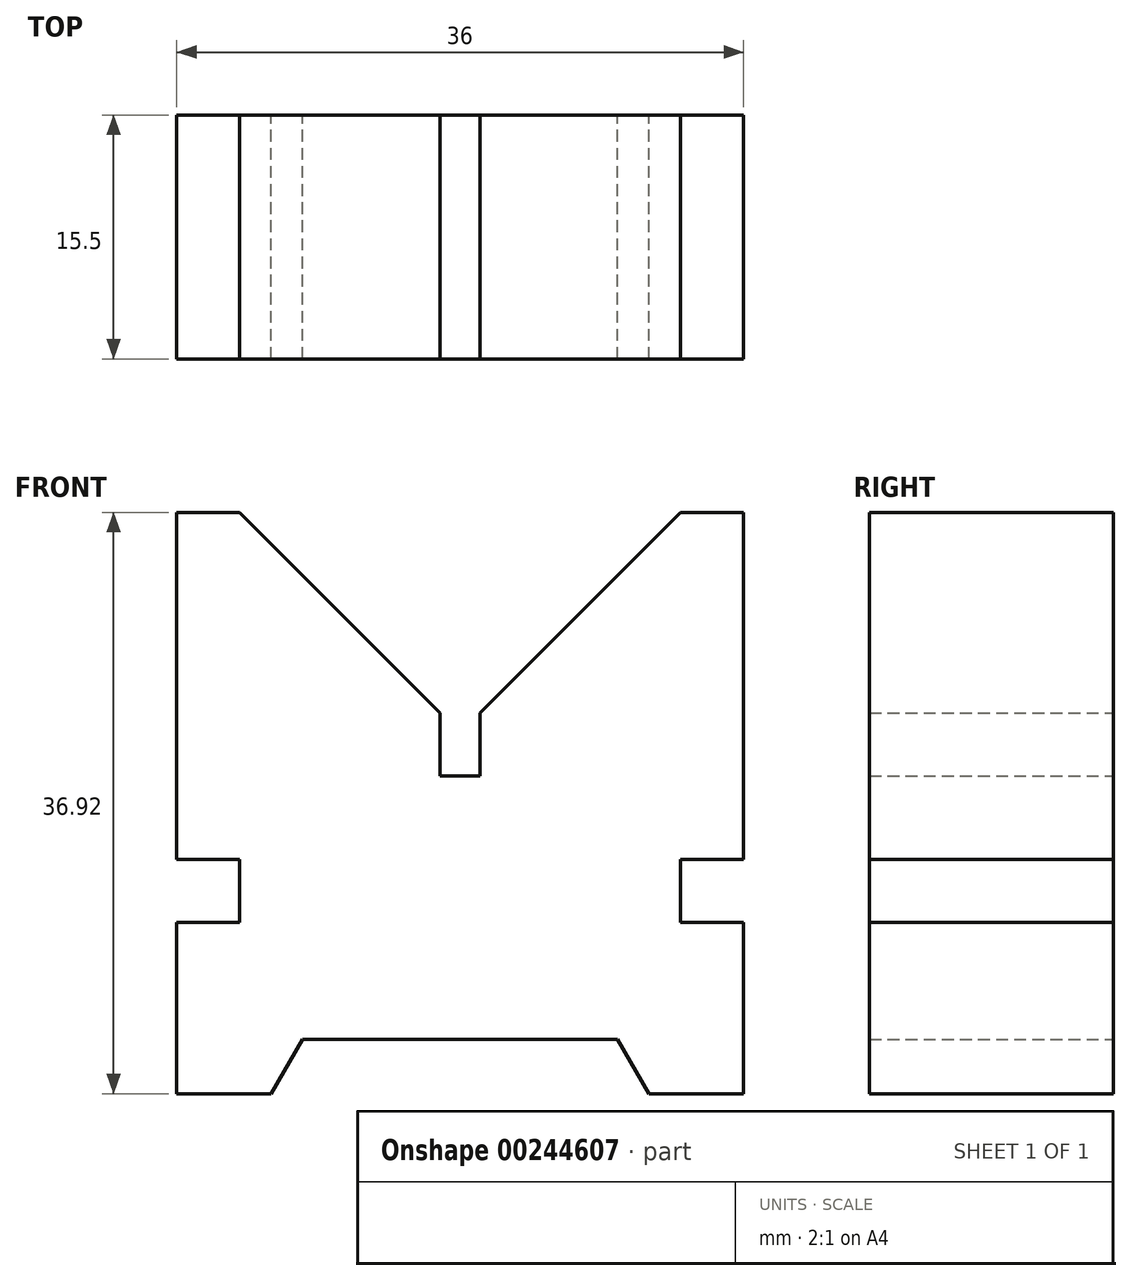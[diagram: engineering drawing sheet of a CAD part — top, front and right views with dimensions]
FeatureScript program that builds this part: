
annotation { "Feature Type Name" : "Feature", "Feature Type Description" : "" }
export const myFeature = defineFeature(function(context is Context, id is Id, definition is map)
    precondition{}
    {
        {
            var Q0;
            Q0=qCreatedBy(makeId("Front.planeOp"),FACE);
            var sketch = newSketch(context, id + "F0", { "sketchPlane" : qUnion([Q0])});
            skLineSegment(sketch, "E0.bottom", {"start": v(1.27, 0) * mm, "end": v(2.54, 0) * mm});
            skLineSegment(sketch, "E0.right", {"start": v(2.54, 0) * mm, "end": v(2.54, 4) * mm});
            skLineSegment(sketch, "E1", {"start": v(2.54, 4) * mm, "end": v(15.27, 16.73) * mm});
            skLineSegment(sketch, "E2", {"start": v(15.27, 16.73) * mm, "end": v(19.27, 16.73) * mm});
            skLineSegment(sketch, "E3", {"start": v(19.27, 16.73) * mm, "end": v(19.27, -5.32) * mm});
            skLineSegment(sketch, "E4", {"start": v(19.27, -5.32) * mm, "end": v(15.27, -5.32) * mm});
            skLineSegment(sketch, "E5", {"start": v(15.27, -5.32) * mm, "end": v(15.27, -9.32) * mm});
            skLineSegment(sketch, "E6", {"start": v(15.27, -9.32) * mm, "end": v(19.27, -9.32) * mm});
            skLineSegment(sketch, "E7", {"start": v(19.27, -9.32) * mm, "end": v(19.27, -20.2) * mm});
            skLineSegment(sketch, "E8", {"start": v(19.27, -20.2) * mm, "end": v(13.27, -20.2) * mm});
            skLineSegment(sketch, "E9", {"start": v(13.27, -20.2) * mm, "end": v(11.27, -16.73) * mm});
            skLineSegment(sketch, "E10", {"start": v(11.27, -16.73) * mm, "end": v(1.27, -16.73) * mm});
            skPoint(sketch, "E10.endSnap0", {"position": v(1.27, 0) * mm});
            skPoint(sketch, "E0.left.start.orphan", {"position": v(0, 0) * mm});
            skLineSegment(sketch, "E11", {"start": v(1.27, 10) * mm, "end": v(1.27, -23.34) * mm, "construction": true});
            skLineSegment(sketch, "E12.MirrorCS", {"start": v(-12.73, 16.73) * mm, "end": v(-16.73, 16.73) * mm});
            skLineSegment(sketch, "E13.MirrorCS", {"start": v(-16.73, 16.73) * mm, "end": v(-16.73, -5.32) * mm});
            skLineSegment(sketch, "E14.MirrorCS", {"start": v(0, 0) * mm, "end": v(0, 4) * mm});
            skLineSegment(sketch, "E15.MirrorCS", {"start": v(0, 4) * mm, "end": v(-12.73, 16.73) * mm});
            skLineSegment(sketch, "E16.MirrorCS", {"start": v(-16.73, -5.32) * mm, "end": v(-12.73, -5.32) * mm});
            skLineSegment(sketch, "E17.MirrorCS", {"start": v(-12.73, -5.32) * mm, "end": v(-12.73, -9.32) * mm});
            skLineSegment(sketch, "E18.MirrorCS", {"start": v(-12.73, -9.32) * mm, "end": v(-16.73, -9.32) * mm});
            skLineSegment(sketch, "E19.MirrorCS", {"start": v(-16.73, -9.32) * mm, "end": v(-16.73, -20.2) * mm});
            skLineSegment(sketch, "E20.MirrorCS", {"start": v(-16.73, -20.2) * mm, "end": v(-10.73, -20.2) * mm});
            skLineSegment(sketch, "E21.MirrorCS", {"start": v(-10.73, -20.2) * mm, "end": v(-8.73, -16.73) * mm});
            skLineSegment(sketch, "E22.MirrorCS", {"start": v(-8.73, -16.73) * mm, "end": v(1.27, -16.73) * mm});
            skLineSegment(sketch, "E23.MirrorCS", {"start": v(1.27, 0) * mm, "end": v(0, 0) * mm});
            skSolve(sketch);
        }
        {
            var Q0;
            Q0 = qSketchRegion(id + "F0", true);
            extrude(context, id + "F1", {"entities" : qUnion([Q0]), "depth" : 15.5 * mm});
        }
    });
